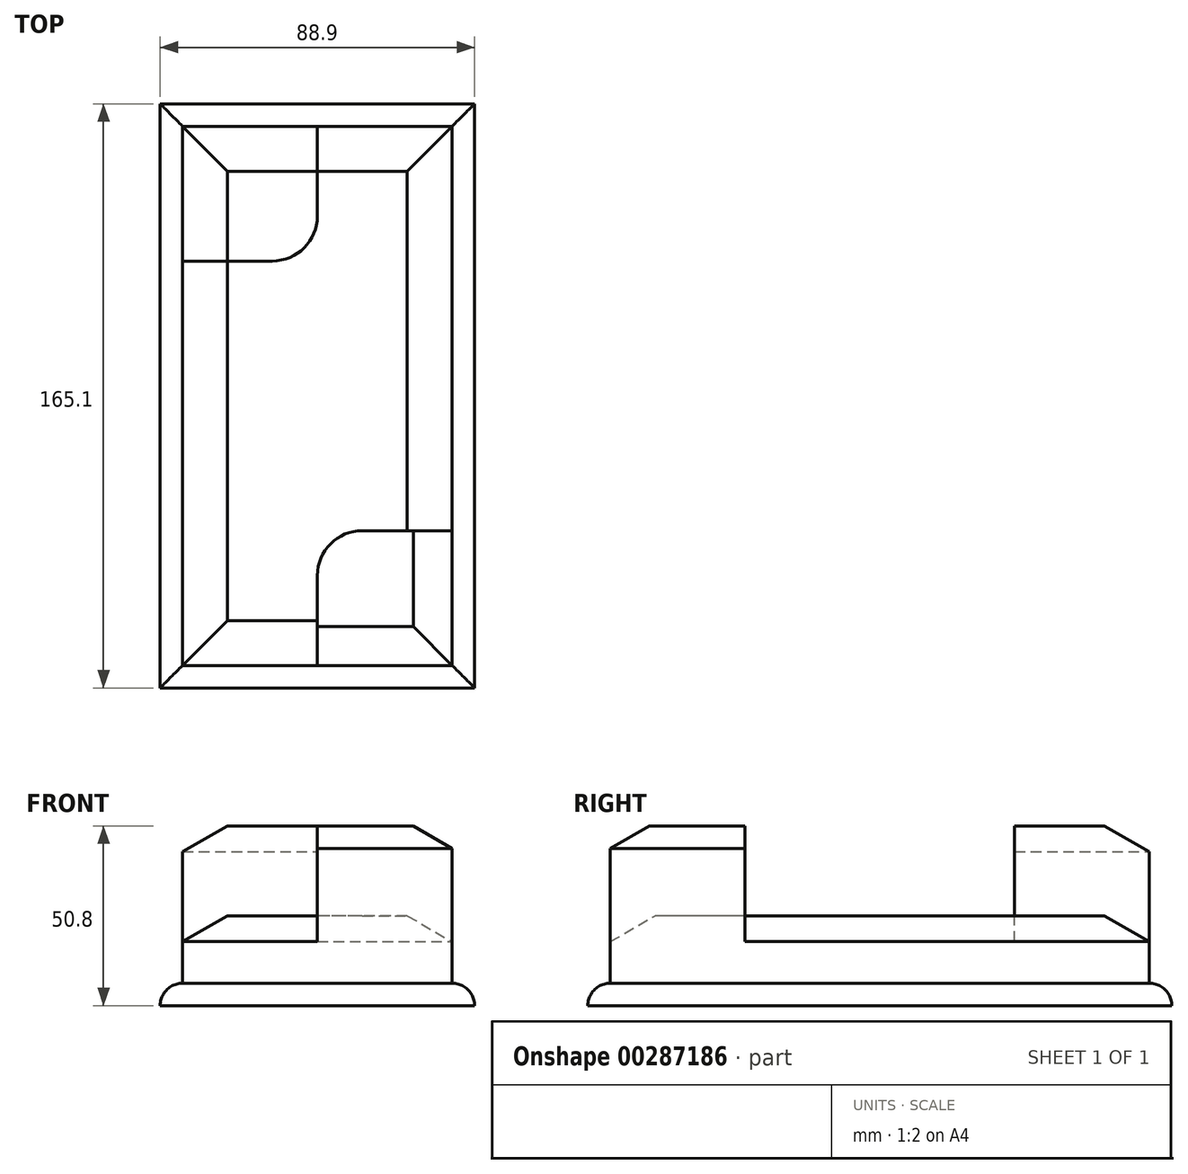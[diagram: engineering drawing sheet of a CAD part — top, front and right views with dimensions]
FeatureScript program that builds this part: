
annotation { "Feature Type Name" : "Feature", "Feature Type Description" : "" }
export const myFeature = defineFeature(function(context is Context, id is Id, definition is map)
    precondition{}
    {
        {
            var Q0;
            Q0=qCreatedBy(makeId("Top.planeOp"),FACE);
            var sketch = newSketch(context, id + "F0", { "sketchPlane" : qUnion([Q0])});
            skLineSegment(sketch, "E0.bottom", {"start": v(38.1, 76.2) * mm, "end": v(-38.1, 76.2) * mm});
            skLineSegment(sketch, "E0.top", {"start": v(38.1, -76.2) * mm, "end": v(-38.1, -76.2) * mm});
            skLineSegment(sketch, "E0.left", {"start": v(38.1, 76.2) * mm, "end": v(38.1, -76.2) * mm});
            skLineSegment(sketch, "E0.right", {"start": v(-38.1, 76.2) * mm, "end": v(-38.1, -76.2) * mm});
            skPoint(sketch, "E0.middle", {"position": v(0, 0) * mm});
            skArc(sketch, "E1", {"start": v(12.71, -38.1) * mm, "mid": v(3.73, -41.82) * mm, "end": v(0.01, -50.8) * mm});
            skArc(sketch, "E2", {"start": v(-12.7, 38.1) * mm, "mid": v(-3.72, 41.82) * mm, "end": v(0, 50.8) * mm});
            skPoint(sketch, "E3.orphan", {"position": v(0, 38.1) * mm});
            skPoint(sketch, "E4.right.end.orphan", {"position": v(0, -38.1) * mm});
            skLineSegment(sketch, "E5", {"start": v(0.01, -50.8) * mm, "end": v(0.01, -76.2) * mm});
            skLineSegment(sketch, "E6", {"start": v(44.45, -82.55) * mm, "end": v(-44.45, -82.55) * mm});
            skLineSegment(sketch, "E7", {"start": v(-44.45, -82.55) * mm, "end": v(-44.45, 82.55) * mm});
            skLineSegment(sketch, "E8", {"start": v(-44.45, 82.55) * mm, "end": v(44.45, 82.55) * mm});
            skLineSegment(sketch, "E9", {"start": v(44.45, 82.55) * mm, "end": v(44.45, -82.55) * mm});
            skLineSegment(sketch, "E10", {"start": v(-12.7, 38.1) * mm, "end": v(-38.1, 38.1) * mm});
            skLineSegment(sketch, "E11", {"start": v(0, 50.8) * mm, "end": v(0, 76.2) * mm});
            skLineSegment(sketch, "E12", {"start": v(12.71, -38.1) * mm, "end": v(38.1, -38.1) * mm});
            skSolve(sketch);
        }
        {
            var Q0;
            Q0=makeQuery(id+"F0.imprint","IMPRINT",FACE,{"disambiguationData":[TD([[makeQuery(id+"F0.imprint","IMPRINT",EDGE,{"derivedFrom":sQuery(id+"F0.wireOp",EDGE,"E1")}),-1.0]])]});
            extrude(context, id + "F1", {"entities" : qUnion([Q0]), "depth" : 25.4 * mm});
        }
        {
            var Q0;
            Q0=makeQuery(id+"F0.imprint","IMPRINT",FACE,{"disambiguationData":[TD([[makeQuery(id+"F0.imprint","IMPRINT",EDGE,{"derivedFrom":sQuery(id+"F0.wireOp",EDGE,"E6")}),-1.0]])]});
            extrude(context, id + "F2", {"entities" : qUnion([Q0]), "operationType" : NewBodyOperationType.ADD, "depth" : 6.35 * mm});
        }
        {
            var Q0;
            Q0=makeQuery(id+"F0.imprint","IMPRINT",FACE,{"disambiguationData":[TD([[makeQuery(id+"F0.imprint","IMPRINT",EDGE,{"derivedFrom":sQuery(id+"F0.wireOp",EDGE,"E2")}),1.0]])]});
            var Q1;
            Q1=makeQuery(id+"F0.imprint","IMPRINT",FACE,{"disambiguationData":[TD([[makeQuery(id+"F0.imprint","IMPRINT",EDGE,{"derivedFrom":sQuery(id+"F0.wireOp",EDGE,"E1")}),1.0]])]});
            extrude(context, id + "F3", {"entities" : qUnion([Q0, Q1]), "operationType" : NewBodyOperationType.ADD, "depth" : 50.8 * mm});
        }
        {
            var Q0;
            Q0=makeQuery(id+"F2.opExtrude","CAP_EDGE",EDGE,{"disambiguationData":[OSD([sQuery(id+"F0.wireOp",EDGE,"E9")])],"isStart":false});
            var Q1;
            Q1=makeQuery(id+"F2.opExtrude","CAP_EDGE",EDGE,{"disambiguationData":[OSD([sQuery(id+"F0.wireOp",EDGE,"E8")])],"isStart":false});
            var Q2;
            Q2=makeQuery(id+"F2.opExtrude","CAP_EDGE",EDGE,{"disambiguationData":[OSD([sQuery(id+"F0.wireOp",EDGE,"E7")])],"isStart":false});
            var Q3;
            Q3=makeQuery(id+"F2.opExtrude","CAP_EDGE",EDGE,{"disambiguationData":[OSD([sQuery(id+"F0.wireOp",EDGE,"E6")])],"isStart":false});
            fillet(context, id + "F4", {"entities" : qUnion([Q0, Q1, Q2, Q3]), "radius" : 6.35 * mm, "tangentPropagation" : true, "allowEdgeOverflow" : false});
        }
        {
            var Q0;
            Q0=makeQuery(id+"F1.opExtrude","CAP_EDGE",EDGE,{"disambiguationData":[OSD([sQuery(id+"F0.wireOp",EDGE,"E0.right")])],"isStart":false});
            var Q1;
            Q1=makeQuery(id+"F1.opExtrude","CAP_EDGE",EDGE,{"disambiguationData":[OSD([sQuery(id+"F0.wireOp",EDGE,"E0.top")])],"isStart":false});
            var Q2;
            Q2=makeQuery(id+"F1.opExtrude","CAP_EDGE",EDGE,{"disambiguationData":[OSD([sQuery(id+"F0.wireOp",EDGE,"E0.bottom")])],"isStart":false});
            var Q3;
            Q3=makeQuery(id+"F1.opExtrude","CAP_EDGE",EDGE,{"disambiguationData":[OSD([sQuery(id+"F0.wireOp",EDGE,"E0.left")])],"isStart":false});
            chamfer(context, id + "F5", {"entities" : qUnion([Q0, Q1, Q2, Q3]), "chamferType" : ChamferType.OFFSET_ANGLE, "width" : 12.7 * mm, "oppositeDirection" : false, "angle" : 30 * degree, "tangentPropagation" : true});
        }
        {
            var Q0;
            Q0=makeQuery(id+"F3.opExtrude","CAP_EDGE",EDGE,{"disambiguationData":[OSD([sQuery(id+"F0.wireOp",EDGE,"E0.right")])],"isStart":false});
            var Q1;
            Q1=makeQuery(id+"F3.opExtrude","CAP_EDGE",EDGE,{"disambiguationData":[OSD([sQuery(id+"F0.wireOp",EDGE,"E0.bottom")])],"isStart":false});
            chamfer(context, id + "F6", {"entities" : qUnion([Q0, Q1]), "chamferType" : ChamferType.OFFSET_ANGLE, "width" : 12.7 * mm, "oppositeDirection" : false, "angle" : 30 * degree, "tangentPropagation" : true});
        }
        {
            var Q0;
            Q0=makeQuery(id+"F3.opExtrude","CAP_EDGE",EDGE,{"disambiguationData":[OSD([sQuery(id+"F0.wireOp",EDGE,"E0.left")])],"isStart":false});
            var Q1;
            Q1=makeQuery(id+"F3.opExtrude","CAP_EDGE",EDGE,{"disambiguationData":[OSD([sQuery(id+"F0.wireOp",EDGE,"E0.top")])],"isStart":false});
            chamfer(context, id + "F7", {"entities" : qUnion([Q0, Q1]), "chamferType" : ChamferType.OFFSET_ANGLE, "width" : 6.35 * mm, "oppositeDirection" : false, "angle" : 60 * degree, "tangentPropagation" : true});
        }
    });
